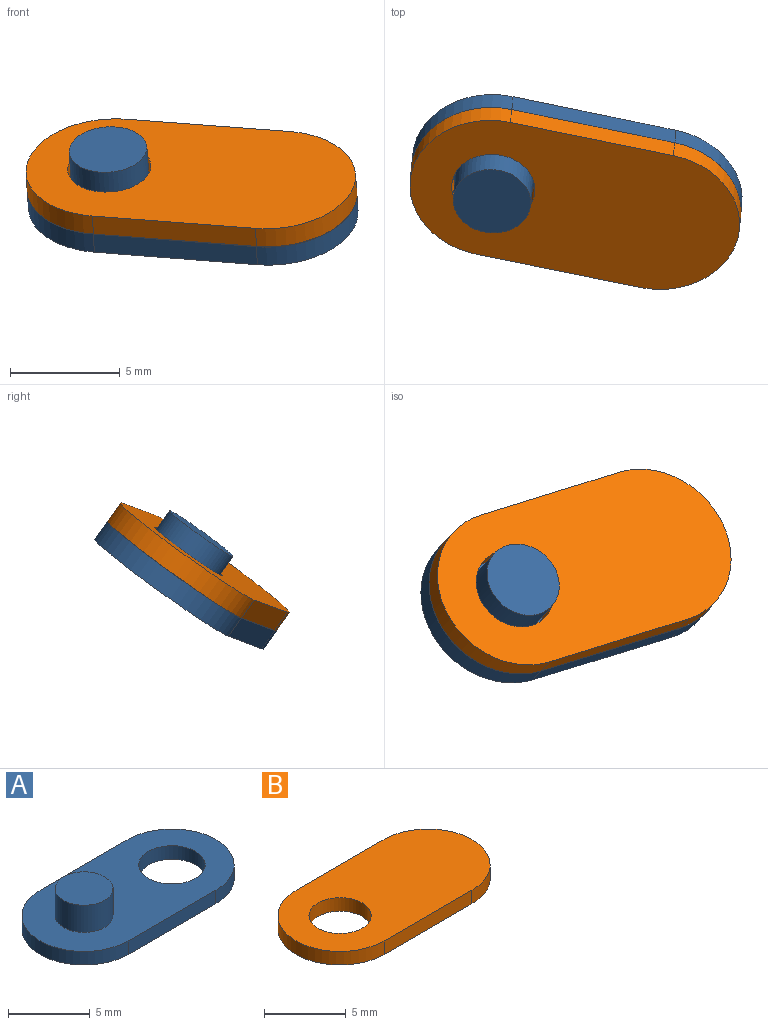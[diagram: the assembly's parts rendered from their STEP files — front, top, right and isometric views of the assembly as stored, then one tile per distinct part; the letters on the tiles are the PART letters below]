
ASSEMBLY  parts=2 mates=1
PART A: 9 faces, bbox 15.2x7.6x3 mm
  f0: cylinder r=3.81mm len=7.62mm, axis (0,0,-1), area 12.2mm2, adj f1,f3,f4,f5
  f1: plane 7.62x1.02mm, normal (0,-1,0), area 7.7mm2, adj f0,f2,f4,f5
  f2: cylinder r=3.81mm len=7.62mm, axis (0,0,-1), area 12.2mm2, adj f1,f3,f4,f5
  f3: plane 7.62x1.02mm, normal (0,1,0), area 7.7mm2, adj f0,f2,f4,f5
  f4: plane 15.24x7.62mm, normal (0,0,1), area 80.8mm2, adj f0,f1,f2,f3,f6,f7
  f5: plane 15.24x7.62mm, normal (0,0,-1), area 90.7mm2, adj f0,f1,f2,f3,f6
  f6: cylinder r=2.03mm len=4.06mm, axis (0,0,1), area 13mm2, adj f4,f5
  f7: cylinder r=1.78mm len=3.56mm, axis (0,0,-1), area 22.7mm2, adj f4,f8
  f8: plane 3.56x3.56mm, normal (0,0,1), area 9.9mm2, adj f7
PART B: 9 faces, bbox 15.2x7.6x2.3 mm
  f0: cylinder r=3.81mm len=7.62mm, axis (0,0,-1), area 12.2mm2, adj f1,f3,f4,f5
  f1: plane 7.62x1.02mm, normal (0,1,0), area 7.7mm2, adj f0,f2,f4,f5
  f2: cylinder r=3.81mm len=7.62mm, axis (0,0,-1), area 12.2mm2, adj f1,f3,f4,f5
  f3: plane 7.62x1.02mm, normal (0,-1,0), area 7.7mm2, adj f0,f2,f4,f5
  f4: plane 15.24x7.62mm, normal (0,0,1), area 92.3mm2, adj f0,f1,f2,f3,f6
  f5: plane 15.24x7.62mm, normal (0,0,-1), area 80.9mm2, adj f0,f1,f2,f3,f6,f8
  f6: cylinder r=1.91mm len=3.81mm, axis (0,0,1), area 12.2mm2, adj f4,f5
  f7: plane 1.27x1.27mm, normal (0,0,-1), area 1.3mm2, adj f8
  f8: torus R=0.64mm, axis (0,0,-1), area 18.1mm2, adj f5,f7
PLACE A rot(axis=(0.94,0.02,-0.33),38deg) t=(17.4,-0.51,11.5)mm
PLACE B rot(axis=(0.94,0.01,-0.33),38deg) t=(17.35,-1.09,12.34)mm
MATE revolute B.f2 <-> A.f7  axis (0.06,0.58,-0.81) through (13.63,-0.33,12.62)mm
